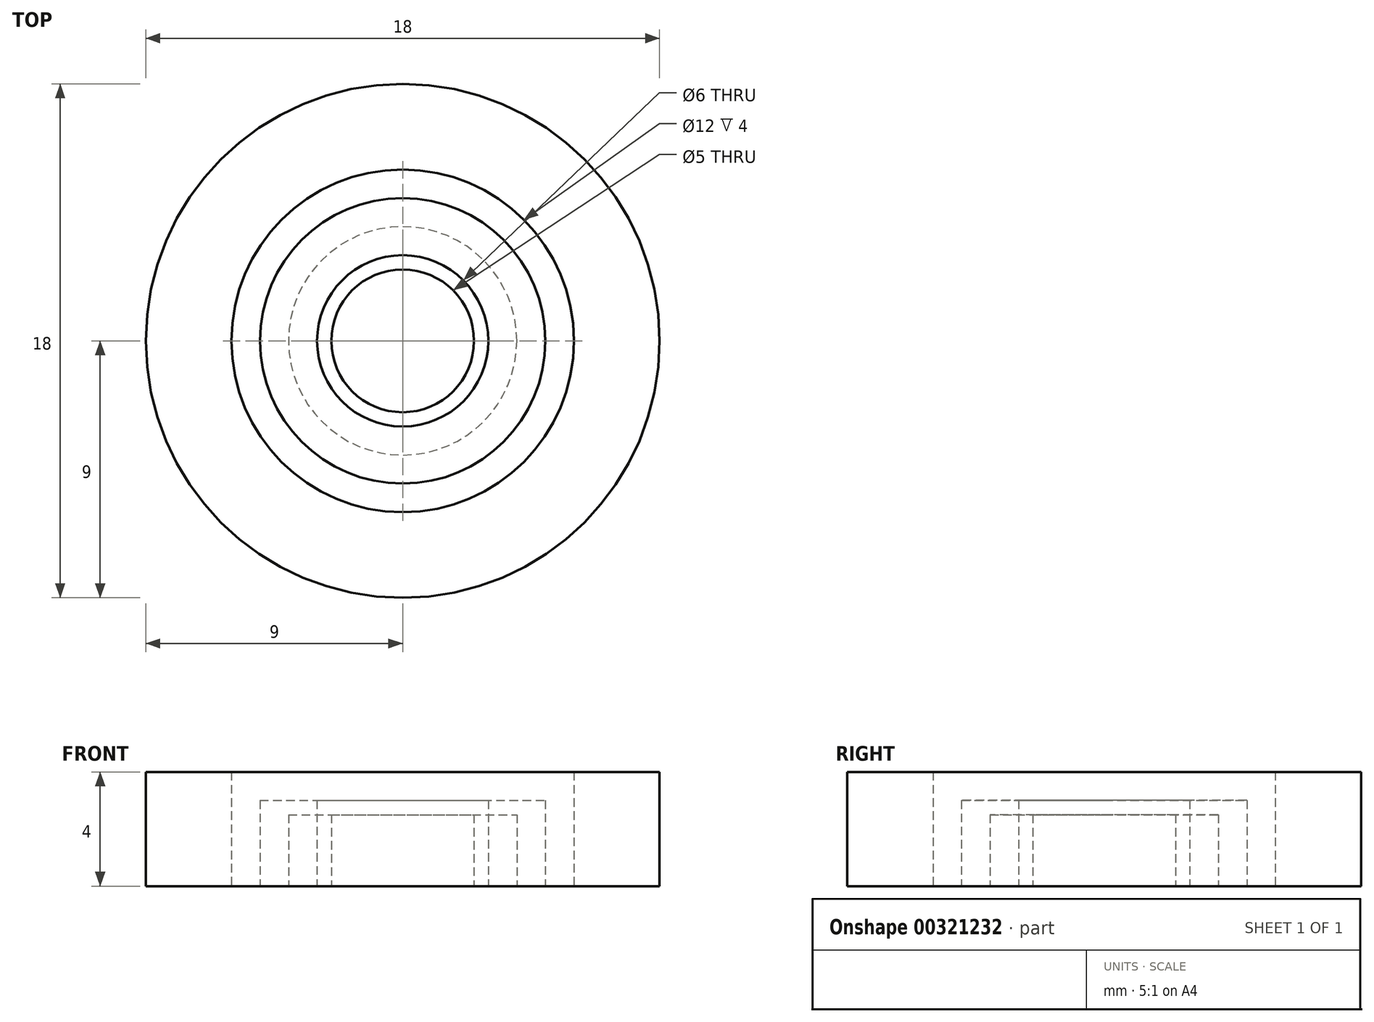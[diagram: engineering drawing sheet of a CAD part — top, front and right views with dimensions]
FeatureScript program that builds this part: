
annotation { "Feature Type Name" : "Feature", "Feature Type Description" : "" }
export const myFeature = defineFeature(function(context is Context, id is Id, definition is map)
    precondition{}
    {
        {
            var Q0;
            Q0=qCreatedBy(makeId("Front.planeOp"),FACE);
            var sketch = newSketch(context, id + "F0", { "sketchPlane" : qUnion([Q0])});
            skLineSegment(sketch, "E0", {"start": v(0, 0) * mm, "end": v(0, 3.45) * mm, "construction": true});
            skLineSegment(sketch, "E1.bottom", {"start": v(-2.5, 0) * mm, "end": v(-4, 0) * mm});
            skLineSegment(sketch, "E1.top", {"start": v(-2.5, 2.5) * mm, "end": v(-4, 2.5) * mm});
            skLineSegment(sketch, "E1.left", {"start": v(-2.5, 0) * mm, "end": v(-2.5, 2.5) * mm});
            skLineSegment(sketch, "E1.right", {"start": v(-4, 0) * mm, "end": v(-4, 2.5) * mm});
            skSolve(sketch);
        }
        {
            var Q0;
            Q0=makeQuery(id+"F0.imprint","IMPRINT",FACE,{"disambiguationData":[TD([[makeQuery(id+"F0.imprint","IMPRINT",EDGE,{"derivedFrom":sQuery(id+"F0.wireOp",EDGE,"E1.bottom")}),-1.0]])]});
            var Q1;
            Q1=sQuery(id+"F0.wireOp",EDGE,"E0");
            revolve(context, id + "F1", {"entities" : qUnion([Q0]), "axis" : qUnion([Q1]), "revolveType" : RevolveType.FULL});
        }
        {
            var Q0;
            Q0=qCreatedBy(makeId("Front.planeOp"),FACE);
            var sketch = newSketch(context, id + "F2", { "sketchPlane" : qUnion([Q0])});
            skLineSegment(sketch, "E2", {"start": v(0, 0) * mm, "end": v(0, 6.43) * mm, "construction": true});
            skLineSegment(sketch, "E3.bottom", {"start": v(-6, 0) * mm, "end": v(-9, 0) * mm});
            skLineSegment(sketch, "E3.top", {"start": v(-6, 4) * mm, "end": v(-9, 4) * mm});
            skLineSegment(sketch, "E3.left", {"start": v(-6, 0) * mm, "end": v(-6, 4) * mm});
            skLineSegment(sketch, "E3.right", {"start": v(-9, 0) * mm, "end": v(-9, 4) * mm});
            skSolve(sketch);
        }
        {
            var Q0;
            Q0 = qSketchRegion(id + "F2", true);
            var Q1;
            Q1=sQuery(id+"F2.wireOp",EDGE,"E2");
            revolve(context, id + "F3", {"entities" : qUnion([Q0]), "axis" : qUnion([Q1]), "revolveType" : RevolveType.FULL});
        }
        {
            var Q0;
            Q0=qCreatedBy(makeId("Front.planeOp"),FACE);
            var sketch = newSketch(context, id + "F4", { "sketchPlane" : qUnion([Q0])});
            skLineSegment(sketch, "E4", {"start": v(0, 0) * mm, "end": v(0, 3.26) * mm, "construction": true});
            skLineSegment(sketch, "E5.bottom", {"start": v(-3, 0) * mm, "end": v(-5, 0) * mm});
            skLineSegment(sketch, "E5.top", {"start": v(-3, 3) * mm, "end": v(-5, 3) * mm});
            skLineSegment(sketch, "E5.left", {"start": v(-3, 0) * mm, "end": v(-3, 3) * mm});
            skLineSegment(sketch, "E5.right", {"start": v(-5, 0) * mm, "end": v(-5, 3) * mm});
            skSolve(sketch);
        }
        {
            var Q0;
            Q0=makeQuery(id+"F4.imprint","IMPRINT",FACE,{"disambiguationData":[TD([[makeQuery(id+"F4.imprint","IMPRINT",EDGE,{"derivedFrom":sQuery(id+"F4.wireOp",EDGE,"E5.bottom")}),-1.0]])]});
            var Q1;
            Q1=sQuery(id+"F4.wireOp",EDGE,"E4");
            revolve(context, id + "F5", {"entities" : qUnion([Q0]), "axis" : qUnion([Q1]), "revolveType" : RevolveType.FULL});
        }
    });
